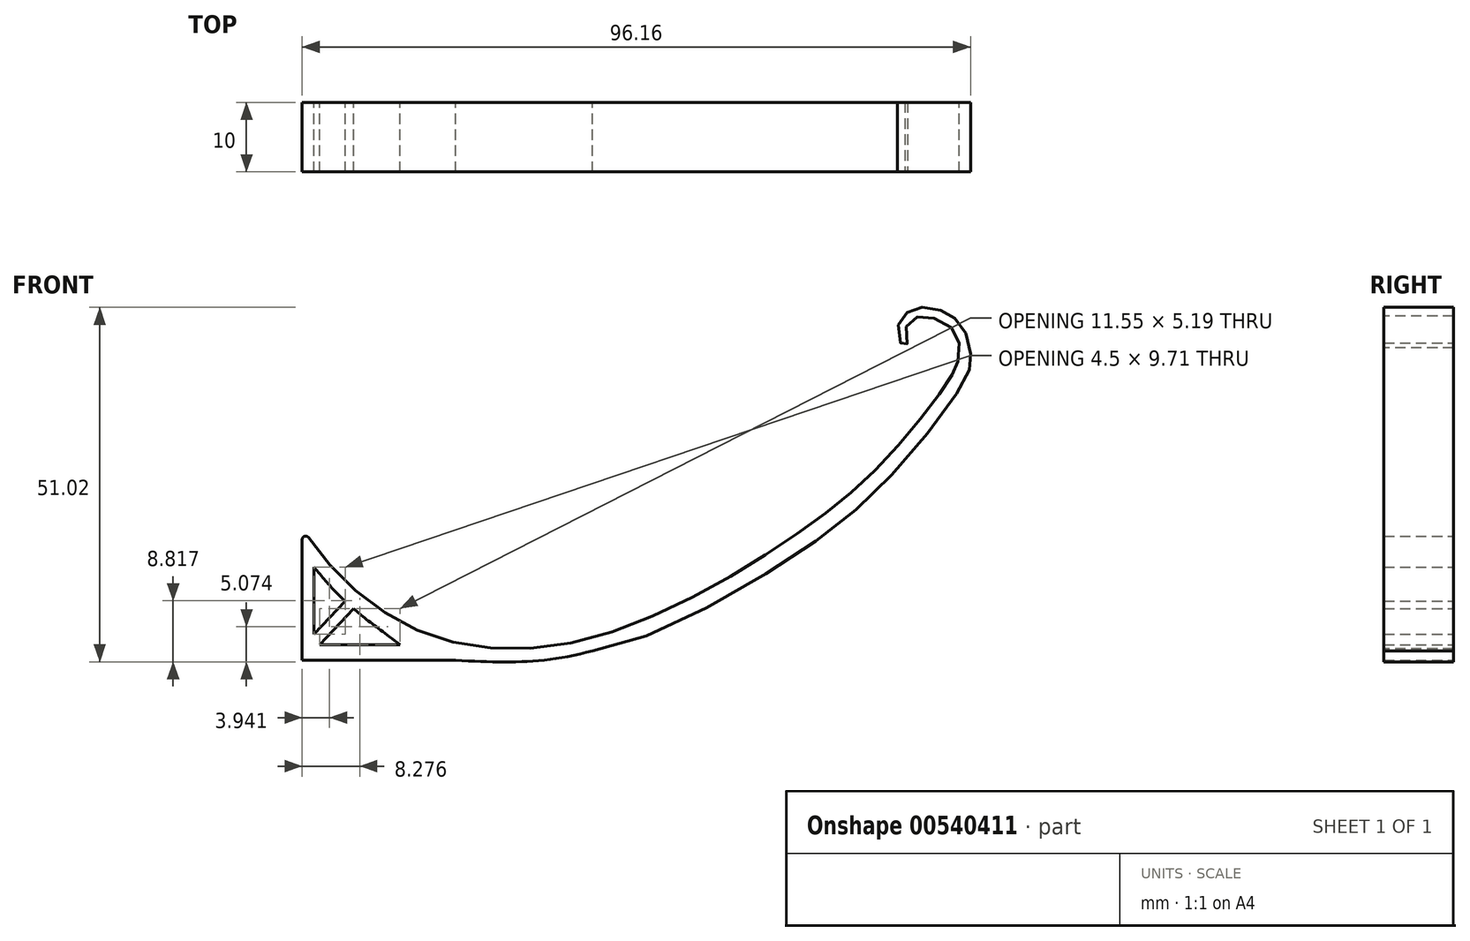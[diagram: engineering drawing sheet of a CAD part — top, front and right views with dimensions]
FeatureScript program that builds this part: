
annotation { "Feature Type Name" : "Feature", "Feature Type Description" : "" }
export const myFeature = defineFeature(function(context is Context, id is Id, definition is map)
    precondition{}
    {
        {
            var Q0;
            Q0=qCreatedBy(makeId("Front.planeOp"),FACE);
            var sketch = newSketch(context, id + "F0", { "sketchPlane" : qUnion([Q0])});
            skFitSpline(sketch, "E0", {"points": [v(-49.54, -63.35) * mm, v(-33.6, -77.79) * mm, v(-8.28, -79.28) * mm, v(19.43, -65.67) * mm, v(34.63, -53.25) * mm, v(44.06, -41.14) * mm, v(44.96, -36.74) * mm], "startDerivative": vector(59.29, -93.56) * mm, "endDerivative": vector(0, 89.69) * mm});
            skFitSpline(sketch, "E1", {"points": [v(44.96, -36.74) * mm, v(43.94, -34.58) * mm, v(41.46, -33.16) * mm, v(39.15, -32.92) * mm, v(37.74, -33.93) * mm, v(37.2, -35.28) * mm, v(37.5, -37.4) * mm, v(36.56, -36.74) * mm, v(36.2, -34.22) * mm, v(37.15, -32.63) * mm, v(38.62, -31.74) * mm, v(41.22, -31.74) * mm, v(43.47, -32.57) * mm, v(44.96, -33.8) * mm, v(46.42, -36.74) * mm, v(46.6, -39.65) * mm, v(46.16, -41.44) * mm, v(36.14, -54.8) * mm, v(20.1, -68.08) * mm, v(-7.79, -81.02) * mm], "startDerivative": vector(-17.55, 56.94) * mm, "endDerivative": vector(-158.92, -18.42) * mm});
            skLineSegment(sketch, "E2", {"start": v(-49.54, -63.35) * mm, "end": v(-49.54, -82.4) * mm});
            skLineSegment(sketch, "E3", {"start": v(-49.54, -82.4) * mm, "end": v(-27.47, -82.4) * mm});
            skFitSpline(sketch, "E4", {"points": [v(-27.47, -82.4) * mm, v(-7.79, -81.02) * mm], "startDerivative": vector(21.55, -1) * mm, "endDerivative": vector(20.96, 5.87) * mm});
            skLineSegment(sketch, "E5", {"start": v(-47.85, -68.95) * mm, "end": v(-47.85, -80.14) * mm});
            skLineSegment(sketch, "E6", {"start": v(-47.85, -80.14) * mm, "end": v(-35.49, -80.14) * mm});
            skFitSpline(sketch, "E7", {"points": [v(-47.85, -68.95) * mm, v(-35.49, -80.14) * mm], "startDerivative": vector(12.1, -14.8) * mm, "endDerivative": vector(19.72, -14.77) * mm});
            skLineSegment(sketch, "E8", {"start": v(-47.85, -78.66) * mm, "end": v(-43.35, -73.88) * mm});
            skLineSegment(sketch, "E9", {"start": v(-47.04, -80.14) * mm, "end": v(-42.16, -74.95) * mm});
            skSolve(sketch);
        }
        {
            var Q0;
            {var subQ0=sQuery(id+"F0.wireOp",EDGE,"E8");Q0=makeQuery(id+"F0.imprint","IMPRINT",FACE,{"disambiguationData":[TD([[makeQuery(id+"F0.imprint","IMPRINT",EDGE,{"derivedFrom":subQ0}),-1.0]])]});}
            var Q1;
            Q1=makeQuery(id+"F0.imprint","IMPRINT",FACE,{"disambiguationData":[TD([[makeQuery(id+"F0.imprint","IMPRINT",EDGE,{"derivedFrom":sQuery(id+"F0.wireOp",EDGE,"E0")}),-1.0]])]});
            extrude(context, id + "F1", {"entities" : qUnion([Q0, Q1]), "depth" : 10 * mm, "offsetDistance" : 25 * mm});
        }
        {
            var Q0;
            Q0=makeQuery(id+"F1.opExtrude","SWEPT_EDGE",EDGE,{"disambiguationData":[OSD([sQuery(id+"F0.wireOp",EDGE,"E0"),sQuery(id+"F0.wireOp",EDGE,"E2")])]});
            fillet(context, id + "F2", {"entities" : qUnion([Q0]), "radius" : 0.5 * mm, "tangentPropagation" : true, "allowEdgeOverflow" : false});
        }
    });
